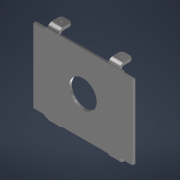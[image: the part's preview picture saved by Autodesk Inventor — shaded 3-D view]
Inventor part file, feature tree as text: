
AUTODESK INVENTOR PART (.ipt)
format: ipt  version: 2022 (Build 260153000, 153)  size: 508,416 bytes
history: native  units: mm
features: sketch x5, other x5, projected_geometry x5, sheet_metal_op x3, chamfer x1, hole x1, extrude x1, reference x1
ambient origin geometry x8: Origin, YZ Plane, XZ Plane, XY Plane, X Axis, Y Axis, Z Axis, Center Point
bodies: Body1 (feature_tree)
feature tree (22):
  sketch  "Sketch1"  dims[d1=20.0mm d4=20.0mm]
  sheet_metal_op  "Face1"
  sketch  "Sketch3"  dims[d5=5.0mm d18=5.0mm]
  sheet_metal_op  "Fold4"
  sheet_metal_op  "Fold5"
  chamfer  "Corner Round1"
  hole  "Hole2"  [1 undecoded]
  extrude  "Extrusion2"  Depth=5.0mm
  reference  "Reference1"
  other  "Plate1"
  projected_geometry  "Projected Loop4"
  sketch  "Sketch4"  dims[d26=110.0mm]
  projected_geometry  "Projected Loop5"
  projected_geometry  "Projected Loop6"
  projected_geometry  "Projected Loop7"
  sketch  "Sketch5"  dims[d27=25.0mm]
  sketch  "Sketch6"  dims[d37=2.0mm d38=2.0mm d39=2.0mm d40=2.0mm d41=2.0mm d42=5.0mm d43=2.5mm d44=10.0mm d45=5.0mm d46=90.0deg d47=5.0mm d48=2.0mm d49=5.0mm d50=2.5mm d51=10.0mm d52=5.0mm d53=90.0deg d54=5.0mm d56=4.5mm d57=6.0mm d58=13.0mm d59=1.0mm d60=90.0deg d61=5.0mm d62=20.594885mm d63=11.5mm d64=50.0mm d65=5.0mm d66=0.0mm d72=0.01mm d73=0.0mm]
  projected_geometry  "Projected Loop8"
  other  "Cut1"
  other  "SistemaElevacionV2.iam"
  other  "Soporte:1"
  other  "Definition1"
note: 1 required parameter value undecoded (feature->parameter linkage not recoverable at this tier; creation-order binding heuristic only, values carry confidence <= 0.55)
